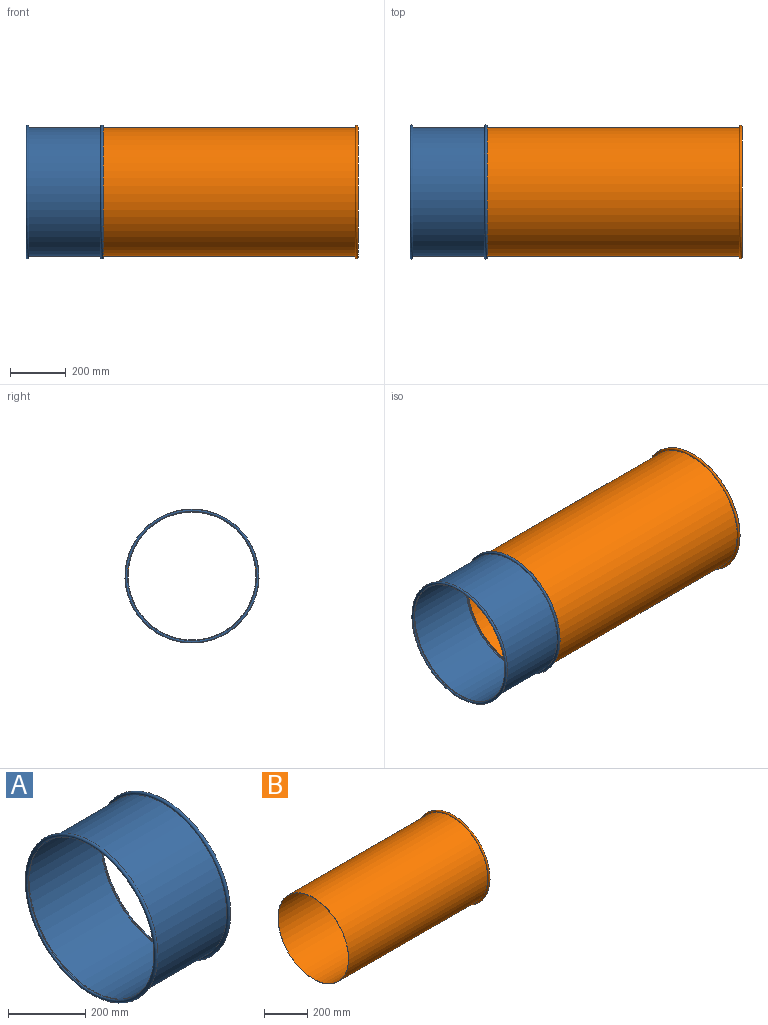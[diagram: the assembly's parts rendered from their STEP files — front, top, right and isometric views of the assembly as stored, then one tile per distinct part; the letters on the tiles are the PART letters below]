
ASSEMBLY  parts=2 mates=1
PART A: 8 faces, bbox 271.1x519.6x519.6 mm
  f0: torus R=234.95mm, axis (-1,0,0), area 35599.2mm2, adj f1,f7
  f1: cylinder r=231.14mm len=462.28mm, axis (-1,0,0), area 2826mm2, adj f0,f2
  f2: torus R=234.95mm, axis (-1,0,0), area 41806.6mm2, adj f1,f3
  f3: cylinder r=229.87mm len=459.74mm, axis (-1,0,0), area 384281.9mm2, adj f2,f4
  f4: torus R=234.95mm, axis (-1,0,0), area 41806.6mm2, adj f3,f5
  f5: cylinder r=231.14mm len=462.28mm, axis (-1,0,0), area 2826mm2, adj f4,f6
  f6: torus R=234.95mm, axis (-1,0,0), area 35599.2mm2, adj f5,f7
  f7: cylinder r=230.89mm len=461.77mm, axis (-1,0,0), area 385980.4mm2, adj f0,f6
PART B: 5 faces, bbox 914.4x517.4x517.4 mm
  f0: cylinder r=229.87mm len=906.27mm, axis (-1,0,0), area 1308943mm2, adj f1,f3
  f1: plane 459.74x459.74mm, normal (-1,0,0), area 1464.2mm2, adj f0,f2
  f2: cylinder r=228.85mm len=909.32mm, axis (-1,0,0), area 1307540.4mm2, adj f1,f3
  f3: torus R=233.93mm, axis (-1,0,0), area 42207.9mm2, adj f0,f2
  f4: torus R=233.93mm, axis (-1,0,0), area 37532.4mm2
PLACE A t=(-276.23,0,0)mm
PLACE B rot(axis=(-1,0,0),0deg) t=(-6.99,0,0)mm
MATE slider B.f0 <-> A.f0  axis (1,0,0) through (279.4,0,0)mm
